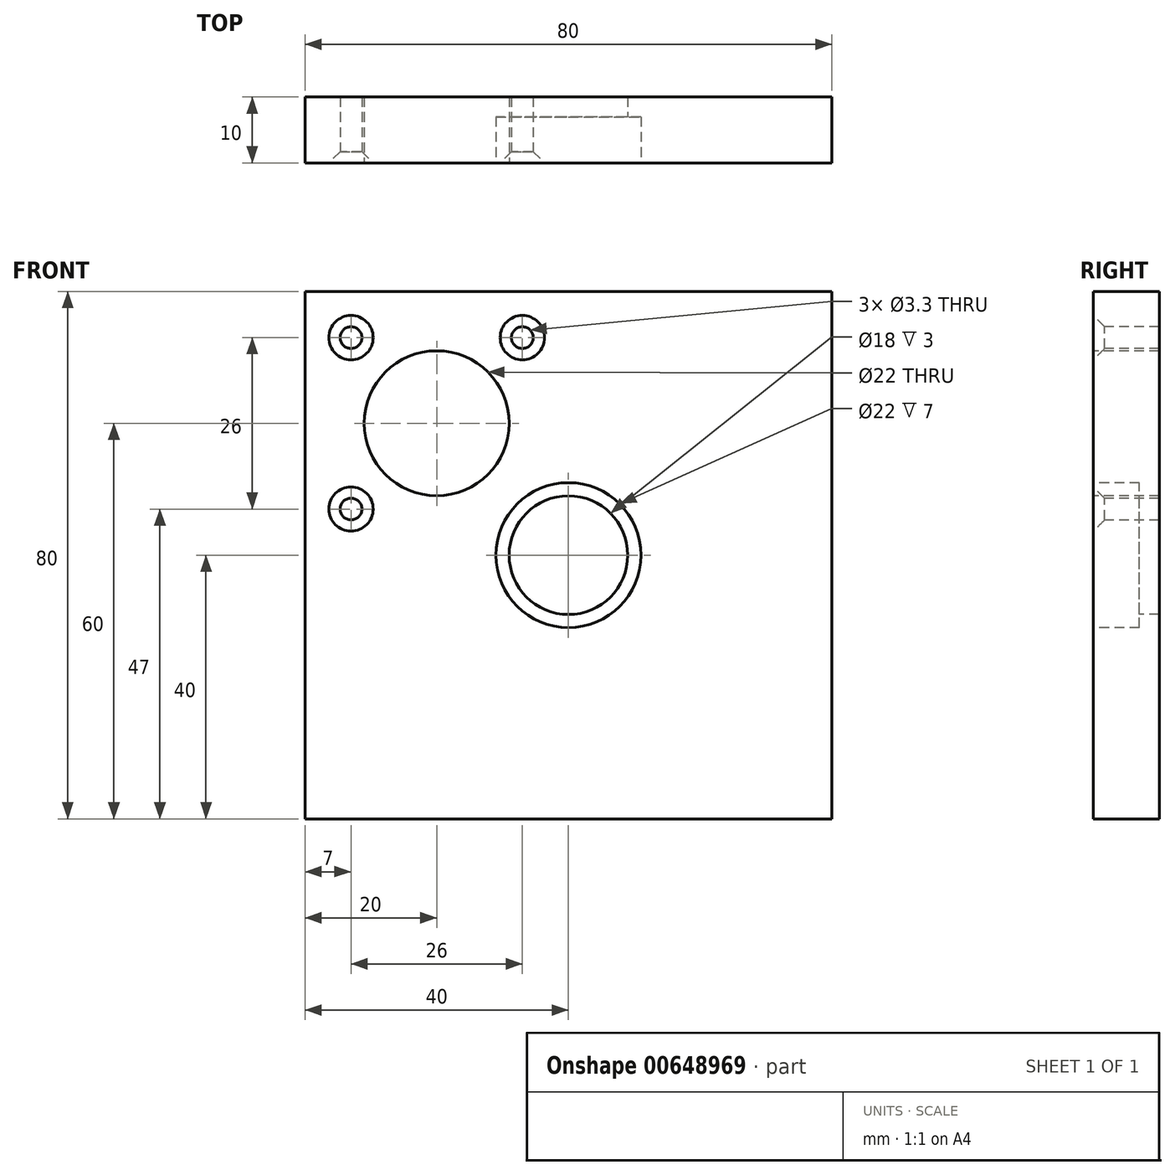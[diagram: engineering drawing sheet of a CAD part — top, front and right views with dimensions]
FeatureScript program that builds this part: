
annotation { "Feature Type Name" : "Feature", "Feature Type Description" : "" }
export const myFeature = defineFeature(function(context is Context, id is Id, definition is map)
    precondition{}
    {
        {
            var Q0;
            Q0=qCreatedBy(makeId("Front.planeOp"),FACE);
            var sketch = newSketch(context, id + "F0", { "sketchPlane" : qUnion([Q0])});
            skLineSegment(sketch, "E0.bottom", {"start": v(-40, 40) * mm, "end": v(40, 40) * mm});
            skLineSegment(sketch, "E0.top", {"start": v(-40, -40) * mm, "end": v(40, -40) * mm});
            skLineSegment(sketch, "E0.left", {"start": v(-40, 40) * mm, "end": v(-40, -40) * mm});
            skLineSegment(sketch, "E0.right", {"start": v(40, 40) * mm, "end": v(40, -40) * mm});
            skPoint(sketch, "E0.middle", {"position": v(0, 0) * mm});
            skSolve(sketch);
        }
        {
            var Q0;
            Q0 = qSketchRegion(id + "F0", true);
            extrude(context, id + "F1", {"entities" : qUnion([Q0]), "depth" : 10 * mm, "offsetDistance" : 25 * mm});
        }
        {
            var Q0;
            Q0=makeQuery(id+"F1.opExtrude","CAP_FACE",FACE,{"disambiguationData":[OSD([sQuery(id+"F0.wireOp",EDGE,"E0.bottom"),sQuery(id+"F0.wireOp",EDGE,"E0.top"),sQuery(id+"F0.wireOp",EDGE,"E0.left"),sQuery(id+"F0.wireOp",EDGE,"E0.right")])],"isStart":false});
            var sketch = newSketch(context, id + "F2", { "sketchPlane" : qUnion([Q0])});
            skLineSegment(sketch, "E1", {"start": v(-40, 0) * mm, "end": v(0, 0) * mm, "construction": true});
            skLineSegment(sketch, "E2", {"start": v(0, 0) * mm, "end": v(0, 40) * mm, "construction": true});
            skCircle(sketch, "E3", {"center": v(-20, 20) * mm, "radius": 11 * mm});
            skPoint(sketch, "E4", {"position": v(-33, 33) * mm});
            skPoint(sketch, "E5.1.0", {"position": v(-33, 7) * mm});
            skPoint(sketch, "E5.2.0", {"position": v(-7, 7) * mm});
            skPoint(sketch, "E5.3.0", {"position": v(-7, 33) * mm});
            skSolve(sketch);
        }
        {
            var Q0;
            Q0=sQuery(id+"F2.wireOp",VERTEX,"E4");
            var Q1;
            Q1=sQuery(id+"F2.wireOp",VERTEX,"E5.3.0");
            var Q2;
            Q2=sQuery(id+"F2.wireOp",VERTEX,"E5.1.0");
            var Q3;
            Q3=makeQuery(id+"F1.opExtrude","SWEPT_BODY",BODY,{"disambiguationData":[OSD([sQuery(id+"F0.wireOp",EDGE,"E0.bottom"),sQuery(id+"F0.wireOp",EDGE,"E0.top"),sQuery(id+"F0.wireOp",EDGE,"E0.left"),sQuery(id+"F0.wireOp",EDGE,"E0.right")])]});
            hole(context, id + "F3", {"style" : HoleStyle.C_SINK, "endStyle" : HoleEndStyle.THROUGH, "standardTappedOrClearance" : lookupTablePath({ "standard" : "ISO", "fit" : "Normal", "size" : "M3", "type" : "Clearance" }), "standardBlindInLast" : lookupTablePath({ "fit" : "Standard", "standard" : "ISO", "size" : "M3", "type" : "Clearance" }), "holeDiameter" : 3.3 * mm, "cSinkDiameter" : 6.72 * mm, "cSinkAngle" : 90 * degree, "majorDiameter" : 5 * mm, "isTappedThrough" : true, "tappedDepth" : 12 * mm, "tapClearance" : 3, "locations" : qUnion([Q0, Q1, Q2]), "scope" : qUnion([Q3])});
        }
        {
            var Q0;
            Q0 = qSketchRegion(id + "F2", true);
            extrude(context, id + "F4", {"entities" : qUnion([Q0]), "operationType" : NewBodyOperationType.REMOVE, "endBound" : BoundingType.THROUGH_ALL, "oppositeDirection" : true, "depth" : 25 * mm, "offsetDistance" : 25 * mm});
        }
        {
            var Q0;
            Q0=makeQuery(id+"F1.opExtrude","CAP_FACE",FACE,{"disambiguationData":[OSD([sQuery(id+"F0.wireOp",EDGE,"E0.bottom"),sQuery(id+"F0.wireOp",EDGE,"E0.top"),sQuery(id+"F0.wireOp",EDGE,"E0.left"),sQuery(id+"F0.wireOp",EDGE,"E0.right")])],"isStart":false});
            var sketch = newSketch(context, id + "F5", { "sketchPlane" : qUnion([Q0])});
            skCircle(sketch, "E6", {"center": v(0, 0) * mm, "radius": 9 * mm});
            skSolve(sketch);
        }
        {
            var Q0;
            Q0 = qSketchRegion(id + "F5", true);
            extrude(context, id + "F6", {"entities" : qUnion([Q0]), "operationType" : NewBodyOperationType.REMOVE, "endBound" : BoundingType.THROUGH_ALL, "oppositeDirection" : true, "depth" : 25 * mm, "offsetDistance" : 25 * mm});
        }
        {
            var Q0;
            Q0=makeQuery(id+"F1.opExtrude","CAP_FACE",FACE,{"disambiguationData":[OSD([sQuery(id+"F0.wireOp",EDGE,"E0.bottom"),sQuery(id+"F0.wireOp",EDGE,"E0.top"),sQuery(id+"F0.wireOp",EDGE,"E0.left"),sQuery(id+"F0.wireOp",EDGE,"E0.right")])],"isStart":false});
            var sketch = newSketch(context, id + "F7", { "sketchPlane" : qUnion([Q0])});
            skCircle(sketch, "E7", {"center": v(0, 0) * mm, "radius": 11 * mm});
            skSolve(sketch);
        }
        {
            var Q0;
            Q0 = qSketchRegion(id + "F7", true);
            extrude(context, id + "F8", {"entities" : qUnion([Q0]), "operationType" : NewBodyOperationType.REMOVE, "oppositeDirection" : true, "depth" : 7 * mm, "offsetDistance" : 25 * mm});
        }
    });
